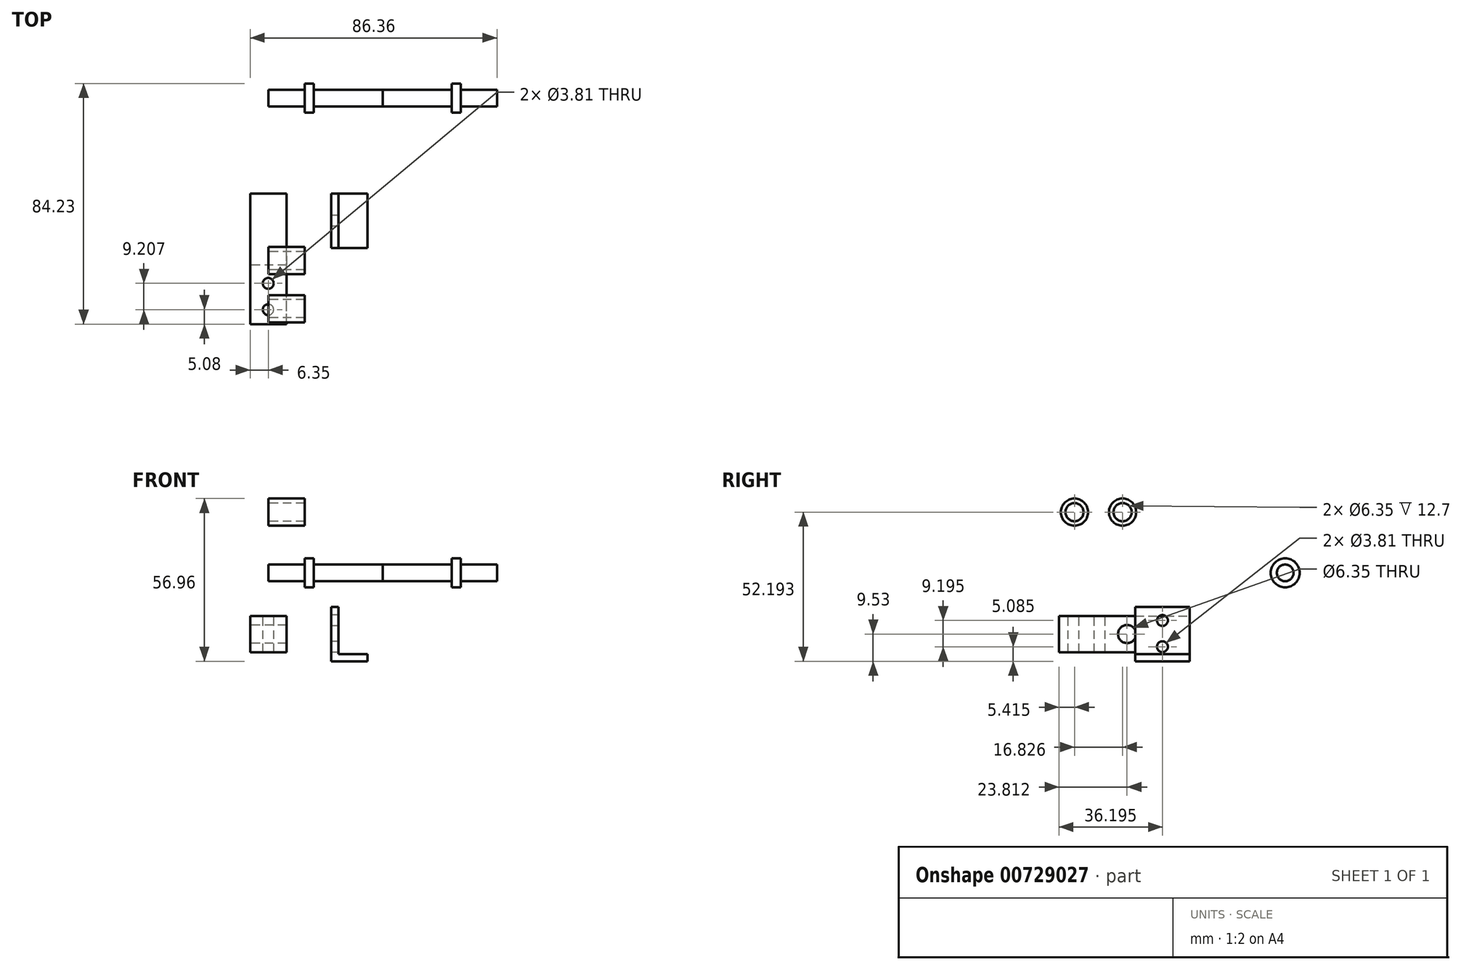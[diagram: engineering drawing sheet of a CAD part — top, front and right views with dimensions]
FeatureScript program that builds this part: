
annotation { "Feature Type Name" : "Feature", "Feature Type Description" : "" }
export const myFeature = defineFeature(function(context is Context, id is Id, definition is map)
    precondition{}
    {
        {
            var Q0;
            Q0=qCreatedBy(makeId("Front.planeOp"),FACE);
            var sketch = newSketch(context, id + "F0", { "sketchPlane" : qUnion([Q0])});
            skLineSegment(sketch, "E0.bottom", {"start": v(6.35, 6.35) * mm, "end": v(-6.35, 6.35) * mm});
            skLineSegment(sketch, "E0.top", {"start": v(6.35, -6.35) * mm, "end": v(-6.35, -6.35) * mm});
            skLineSegment(sketch, "E0.left", {"start": v(6.35, 6.35) * mm, "end": v(6.35, -6.35) * mm});
            skLineSegment(sketch, "E0.right", {"start": v(-6.35, 6.35) * mm, "end": v(-6.35, -6.35) * mm});
            skPoint(sketch, "E0.middle", {"position": v(0, 0) * mm});
            skLineSegment(sketch, "E1.bottom", {"start": v(21.97, 9.53) * mm, "end": v(34.67, 9.53) * mm});
            skLineSegment(sketch, "E1.top", {"start": v(21.97, -9.53) * mm, "end": v(34.67, -9.53) * mm});
            skLineSegment(sketch, "E1.left", {"start": v(21.97, 9.53) * mm, "end": v(21.97, -9.53) * mm});
            skLineSegment(sketch, "E1.right", {"start": v(34.67, 9.53) * mm, "end": v(34.67, -9.52) * mm});
            skPoint(sketch, "E1.middle", {"position": v(28.32, 0) * mm});
            skLineSegment(sketch, "E2.bottom", {"start": v(34.67, 9.53) * mm, "end": v(24.5, 9.53) * mm});
            skLineSegment(sketch, "E2.top", {"start": v(34.67, -6.99) * mm, "end": v(24.5, -6.99) * mm});
            skLineSegment(sketch, "E2.left", {"start": v(34.67, 9.52) * mm, "end": v(34.67, -6.99) * mm});
            skLineSegment(sketch, "E2.right", {"start": v(24.5, 9.52) * mm, "end": v(24.5, -6.99) * mm});
            skSolve(sketch);
        }
        {
            var Q0;
            Q0=makeQuery(id+"F0.imprint","IMPRINT",FACE,{"disambiguationData":[TD([[makeQuery(id+"F0.imprint","IMPRINT",EDGE,{"derivedFrom":sQuery(id+"F0.wireOp",EDGE,"E0.bottom")}),1.0]])]});
            extrude(context, id + "F1", {"entities" : qUnion([Q0]), "depth" : 45.72 * mm, "offsetDistance" : 25.4 * mm});
        }
        {
            var Q0;
            {var subQ1=sQuery(id+"F0.wireOp",EDGE,"E1.top");Q0=makeQuery(id+"F0.imprint","IMPRINT",FACE,{"disambiguationData":[TD([[makeQuery(id+"F0.imprint","IMPRINT",EDGE,{"derivedFrom":subQ1}),1.0]])]});}
            extrude(context, id + "F2", {"entities" : qUnion([Q0]), "depth" : 19.05 * mm, "offsetDistance" : 25.4 * mm});
        }
        {
            var Q0;
            Q0=makeQuery(id+"F2.opExtrude","SWEPT_FACE",FACE,{"disambiguationData":[OSD([sQuery(id+"F0.wireOp",EDGE,"E1.left")])]});
            var sketch = newSketch(context, id + "F3", { "sketchPlane" : qUnion([Q0])});
            skLineSegment(sketch, "E3", {"start": v(9.53, 9.53) * mm, "end": v(9.53, -9.52) * mm});
            skCircle(sketch, "E4", {"center": v(9.53, 4.75) * mm, "radius": 1.9 * mm});
            skCircle(sketch, "E5", {"center": v(9.53, -4.44) * mm, "radius": 1.9 * mm});
            skSolve(sketch);
        }
        {
            var Q0;
            Q0 = qSketchRegion(id + "F3", true);
            extrude(context, id + "F4", {"entities" : qUnion([Q0]), "operationType" : NewBodyOperationType.REMOVE, "oppositeDirection" : true, "depth" : 25.4 * mm, "offsetDistance" : 25.4 * mm});
        }
        {
            var Q0;
            Q0=makeQuery(id+"F1.opExtrude","SWEPT_FACE",FACE,{"disambiguationData":[OSD([sQuery(id+"F0.wireOp",EDGE,"E0.bottom")])]});
            var sketch = newSketch(context, id + "F5", { "sketchPlane" : qUnion([Q0])});
            skLineSegment(sketch, "E6", {"start": v(0, -45.72) * mm, "end": v(0, 0) * mm});
            skCircle(sketch, "E7", {"center": v(0, -40.64) * mm, "radius": 1.9 * mm});
            skCircle(sketch, "E8", {"center": v(0, -31.43) * mm, "radius": 1.9 * mm});
            skSolve(sketch);
        }
        {
            var Q0;
            Q0 = qSketchRegion(id + "F5", true);
            extrude(context, id + "F6", {"entities" : qUnion([Q0]), "operationType" : NewBodyOperationType.REMOVE, "oppositeDirection" : true, "depth" : 25.4 * mm, "offsetDistance" : 25.4 * mm});
        }
        {
            var Q0;
            Q0=makeQuery(id+"F1.opExtrude","SWEPT_FACE",FACE,{"disambiguationData":[OSD([sQuery(id+"F0.wireOp",EDGE,"E0.right")])]});
            var sketch = newSketch(context, id + "F7", { "sketchPlane" : qUnion([Q0])});
            skLineSegment(sketch, "E9", {"start": v(0, 0) * mm, "end": v(45.72, 0) * mm});
            skCircle(sketch, "E10", {"center": v(21.9, 0) * mm, "radius": 3.18 * mm});
            skSolve(sketch);
        }
        {
            var Q0;
            Q0 = qSketchRegion(id + "F7", true);
            extrude(context, id + "F8", {"entities" : qUnion([Q0]), "operationType" : NewBodyOperationType.REMOVE, "oppositeDirection" : true, "depth" : 25.4 * mm, "offsetDistance" : 25.4 * mm});
        }
        {
            var Q0;
            Q0=qCreatedBy(makeId("Right.planeOp"),FACE);
            var sketch = newSketch(context, id + "F9", { "sketchPlane" : qUnion([Q0])});
            skLineSegment(sketch, "E11", {"start": v(-40.3, 42.66) * mm, "end": v(-23.48, 42.66) * mm});
            skCircle(sketch, "E12", {"center": v(-40.3, 42.66) * mm, "radius": 4.76 * mm});
            skCircle(sketch, "E13", {"center": v(-23.48, 42.66) * mm, "radius": 4.76 * mm});
            skCircle(sketch, "E14", {"center": v(-40.3, 42.66) * mm, "radius": 3.18 * mm});
            skCircle(sketch, "E15", {"center": v(-23.48, 42.66) * mm, "radius": 3.18 * mm});
            skSolve(sketch);
        }
        {
            var Q0;
            Q0 = qSketchRegion(id + "F9", true);
            extrude(context, id + "F10", {"entities" : qUnion([Q0]), "depth" : 12.7 * mm, "offsetDistance" : 25.4 * mm});
        }
        {
            var Q0;
            Q0=qCreatedBy(makeId("Right.planeOp"),FACE);
            var sketch = newSketch(context, id + "F11", { "sketchPlane" : qUnion([Q0])});
            skCircle(sketch, "E16", {"center": v(33.43, 21.4) * mm, "radius": 2.92 * mm});
            skSolve(sketch);
        }
        {
            var Q0;
            Q0 = qSketchRegion(id + "F11", true);
            extrude(context, id + "F12", {"entities" : qUnion([Q0]), "depth" : 12.7 * mm, "offsetDistance" : 25.4 * mm});
        }
        {
            var Q0;
            Q0=makeQuery(id+"F12.opExtrude","CAP_FACE",FACE,{"disambiguationData":[OSD([sQuery(id+"F11.wireOp",EDGE,"E16")])],"isStart":false});
            var sketch = newSketch(context, id + "F13", { "sketchPlane" : qUnion([Q0])});
            skCircle(sketch, "E17", {"center": v(33.43, 21.4) * mm, "radius": 5.08 * mm});
            skSolve(sketch);
        }
        {
            var Q0;
            Q0 = qSketchRegion(id + "F13", true);
            extrude(context, id + "F14", {"entities" : qUnion([Q0]), "operationType" : NewBodyOperationType.ADD, "depth" : 3.17 * mm, "offsetDistance" : 25.4 * mm});
        }
        {
            var Q0;
            Q0=makeQuery(id+"F14.opExtrude","CAP_FACE",FACE,{"disambiguationData":[OSD([sQuery(id+"F13.wireOp",EDGE,"E17")])],"isStart":false});
            var sketch = newSketch(context, id + "F15", { "sketchPlane" : qUnion([Q0])});
            skCircle(sketch, "E18", {"center": v(33.43, 21.4) * mm, "radius": 2.92 * mm});
            skSolve(sketch);
        }
        {
            var Q0;
            Q0 = qSketchRegion(id + "F15", true);
            extrude(context, id + "F16", {"entities" : qUnion([Q0]), "operationType" : NewBodyOperationType.ADD, "depth" : 24.13 * mm, "offsetDistance" : 25.4 * mm});
        }
        {
            var Q0;
            Q0=makeQuery(id+"F12.opExtrude","SWEPT_BODY",BODY,{"disambiguationData":[OSD([sQuery(id+"F11.wireOp",EDGE,"E16")])]});
            var Q1;
            Q1=makeQuery(id+"F16.opExtrude","CAP_FACE",FACE,{"disambiguationData":[OSD([sQuery(id+"F15.wireOp",EDGE,"E18")])],"isStart":false});
            mirror(context, id + "F17", {"operationType" : NewBodyOperationType.ADD, "entities" : qUnion([Q0]), "mirrorPlane" : qUnion([Q1])});
        }
    });
